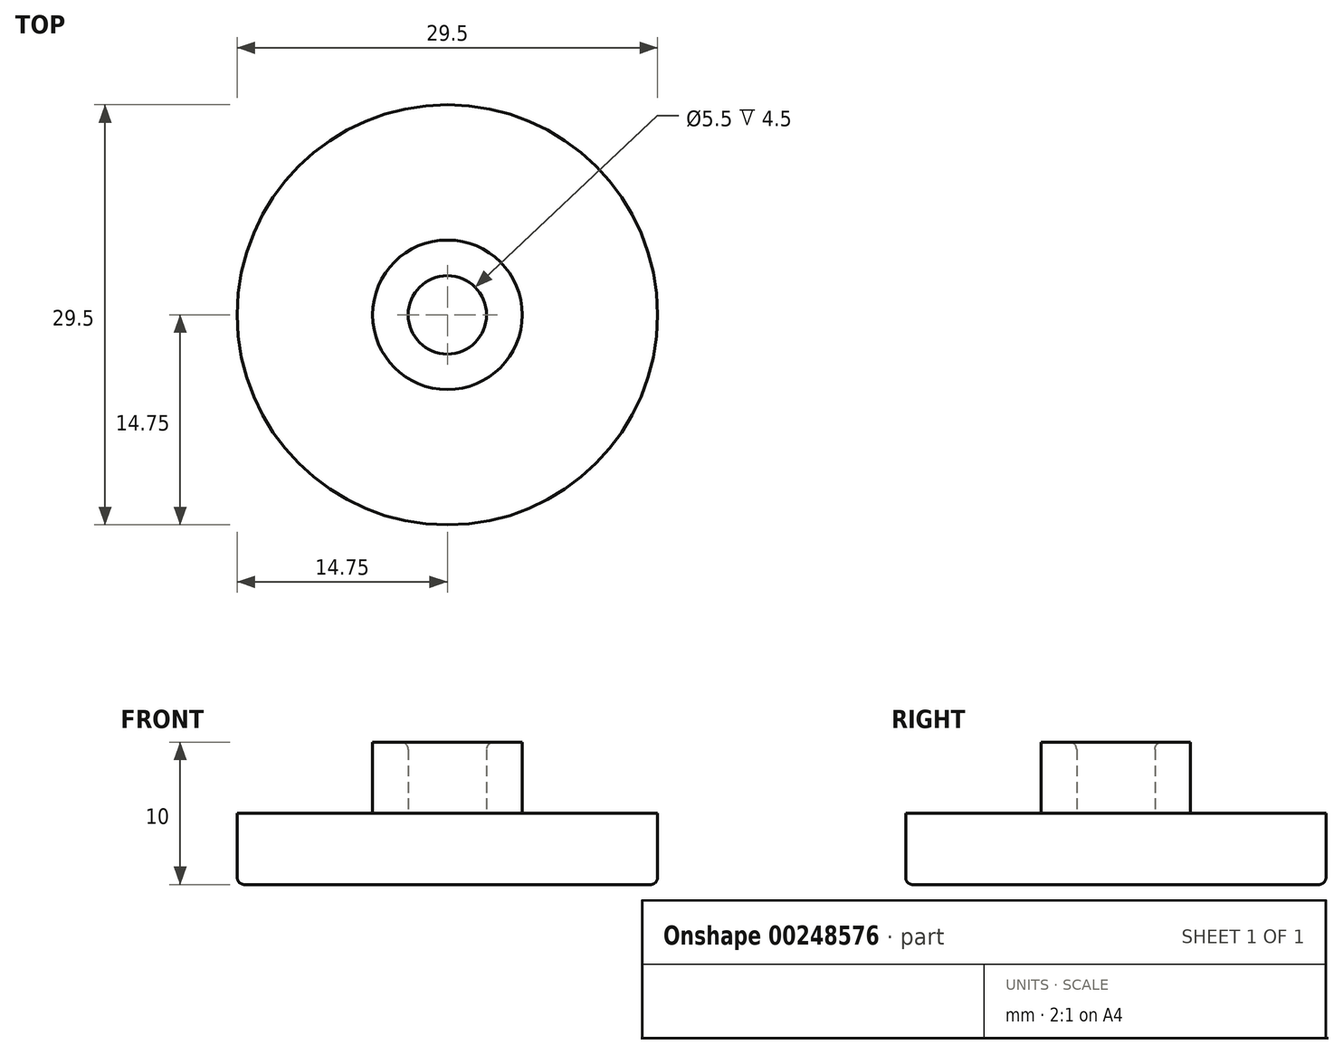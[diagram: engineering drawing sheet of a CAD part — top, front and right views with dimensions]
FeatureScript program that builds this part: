
annotation { "Feature Type Name" : "Feature", "Feature Type Description" : "" }
export const myFeature = defineFeature(function(context is Context, id is Id, definition is map)
    precondition{}
    {
        {
            var Q0;
            Q0=qCreatedBy(makeId("Top.planeOp"),FACE);
            var sketch = newSketch(context, id + "F0", { "sketchPlane" : qUnion([Q0])});
            skCircle(sketch, "E0", {"center": v(0, 0) * mm, "radius": 14.75 * mm});
            skSolve(sketch);
        }
        {
            var Q0;
            Q0 = qSketchRegion(id + "F0", true);
            extrude(context, id + "F1", {"entities" : qUnion([Q0]), "depth" : 5 * mm});
        }
        {
            var Q0;
            Q0=makeQuery(id+"F1.opExtrude","CAP_FACE",FACE,{"disambiguationData":[OSD([sQuery(id+"F0.wireOp",EDGE,"E0")])],"isStart":false});
            var sketch = newSketch(context, id + "F2", { "sketchPlane" : qUnion([Q0])});
            skCircle(sketch, "E1", {"center": v(0, 0) * mm, "radius": 2.75 * mm});
            skCircle(sketch, "E2", {"center": v(0, 0) * mm, "radius": 5.25 * mm});
            skSolve(sketch);
        }
        {
            var Q0;
            Q0 = qSketchRegion(id + "F2", true);
            extrude(context, id + "F3", {"entities" : qUnion([Q0]), "operationType" : NewBodyOperationType.ADD, "depth" : 5 * mm});
        }
        {
            var Q0;
            Q0=makeQuery(id+"F1.opExtrude","CAP_EDGE",EDGE,{"disambiguationData":[OSD([sQuery(id+"F0.wireOp",EDGE,"E0")])],"isStart":true});
            var Q1;
            Q1=makeQuery(id+"F3.opExtrude","CAP_EDGE",EDGE,{"disambiguationData":[OSD([sQuery(id+"F2.wireOp",EDGE,"E1")])],"isStart":false});
            fillet(context, id + "F4", {"entities" : qUnion([Q0, Q1]), "radius" : 0.5 * mm, "tangentPropagation" : true, "allowEdgeOverflow" : false});
        }
    });
